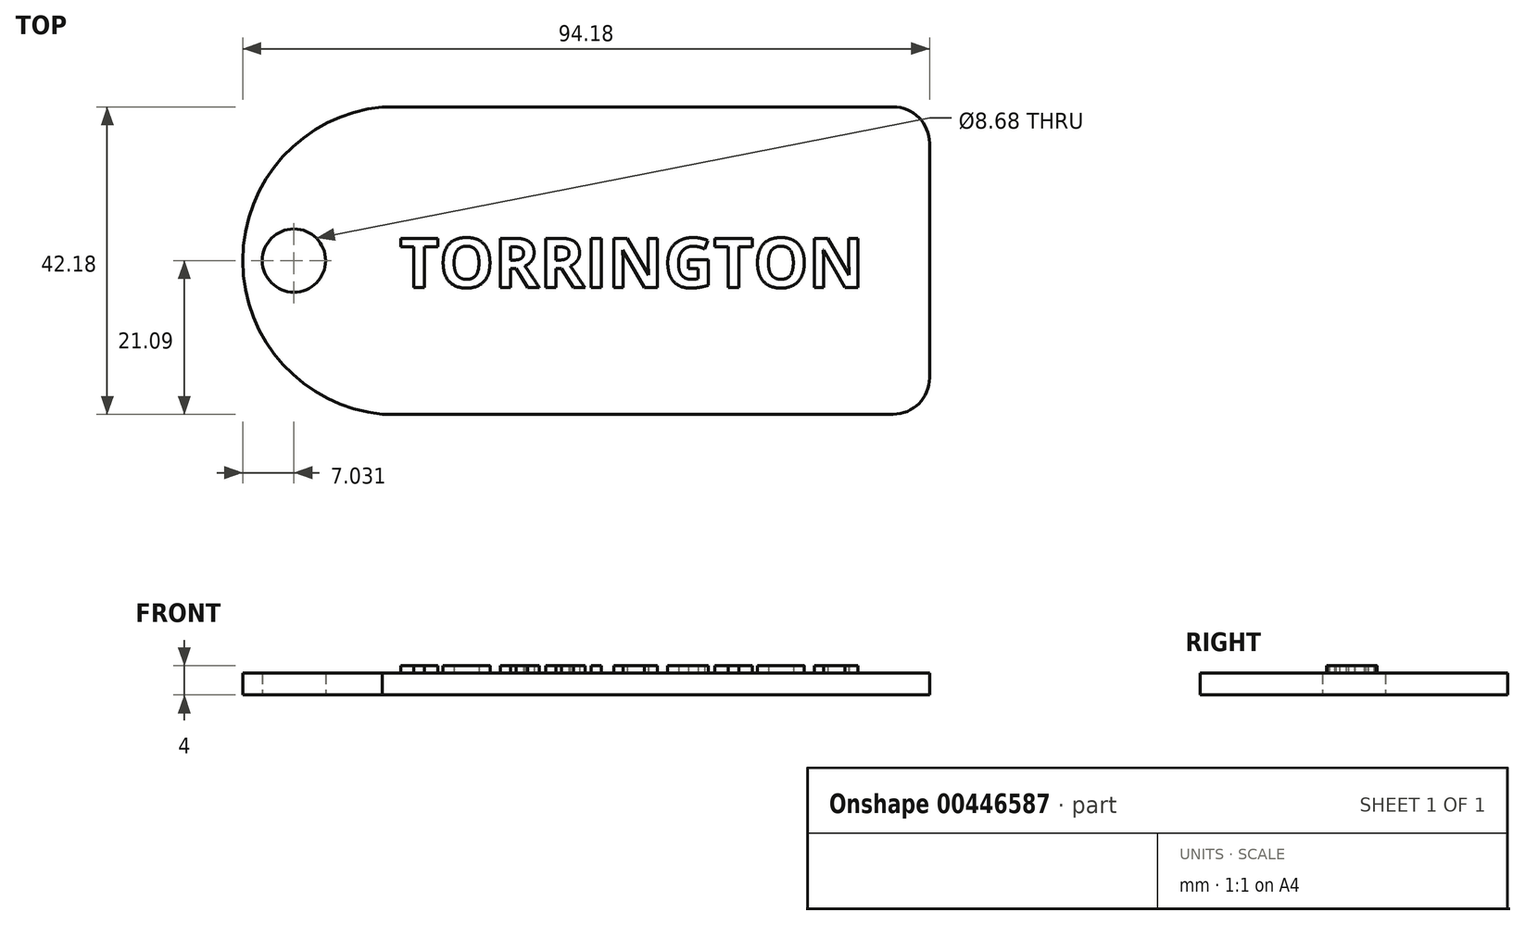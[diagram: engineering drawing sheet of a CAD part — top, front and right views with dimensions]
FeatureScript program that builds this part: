
annotation { "Feature Type Name" : "Feature", "Feature Type Description" : "" }
export const myFeature = defineFeature(function(context is Context, id is Id, definition is map)
    precondition{}
    {
        {
            var Q0;
            Q0=qCreatedBy(makeId("Top.planeOp"),FACE);
            var sketch = newSketch(context, id + "F0", { "sketchPlane" : qUnion([Q0])});
            skLineSegment(sketch, "E0.bottom", {"start": v(32.5, 21.09) * mm, "end": v(-37.5, 21.09) * mm});
            skLineSegment(sketch, "E0.top", {"start": v(32.5, -21.09) * mm, "end": v(-37.5, -21.09) * mm});
            skLineSegment(sketch, "E0.left", {"start": v(37.5, 16.09) * mm, "end": v(37.5, -16.09) * mm});
            skLineSegment(sketch, "E0.right", {"start": v(-37.5, 21.09) * mm, "end": v(-37.5, -21.09) * mm});
            skPoint(sketch, "E0.middle", {"position": v(0, 0) * mm});
            skArc(sketch, "E1", {"start": v(-37.5, 21.09) * mm, "mid": v(-56.67, 0) * mm, "end": v(-37.5, -21.09) * mm});
            skPoint(sketch, "E2.visualSharp", {"position": v(37.5, 21.09) * mm});
            skArc(sketch, "E2.filletArc", {"start": v(37.5, 16.09) * mm, "mid": v(36.04, 19.62) * mm, "end": v(32.5, 21.09) * mm});
            skPoint(sketch, "E3.visualSharp", {"position": v(37.5, -21.09) * mm});
            skArc(sketch, "E3.filletArc", {"start": v(32.5, -21.09) * mm, "mid": v(36.04, -19.62) * mm, "end": v(37.5, -16.09) * mm});
            skCircle(sketch, "E4", {"center": v(-49.64, 0) * mm, "radius": 4.34 * mm});
            skPoint(sketch, "E4.centerSnap0", {"position": v(-37.5, 0) * mm});
            skSolve(sketch);
        }
        {
            var Q0;
            Q0 = qSketchRegion(id + "F0", true);
            extrude(context, id + "F1", {"entities" : qUnion([Q0]), "depth" : 3 * mm});
        }
        {
            var Q0;
            Q0=qCreatedBy(makeId("Top.planeOp"),FACE);
            var sketch = newSketch(context, id + "F2", { "sketchPlane" : qUnion([Q0])});
            skText(sketch, "E5", { "text": "TORRINGTON", "fontName": "OpenSans-Bold.ttf"});
            const initialGuessF2  = {"E5": [-0.0352, -0.00368, 1, 0, 0.0068]};
            skSetInitialGuess(sketch, initialGuessF2);
            skSolve(sketch);
        }
        {
            var Q0;
            Q0 = qSketchRegion(id + "F2", true);
            extrude(context, id + "F3", {"entities" : qUnion([Q0]), "operationType" : NewBodyOperationType.ADD, "depth" : 4 * mm});
        }
    });
